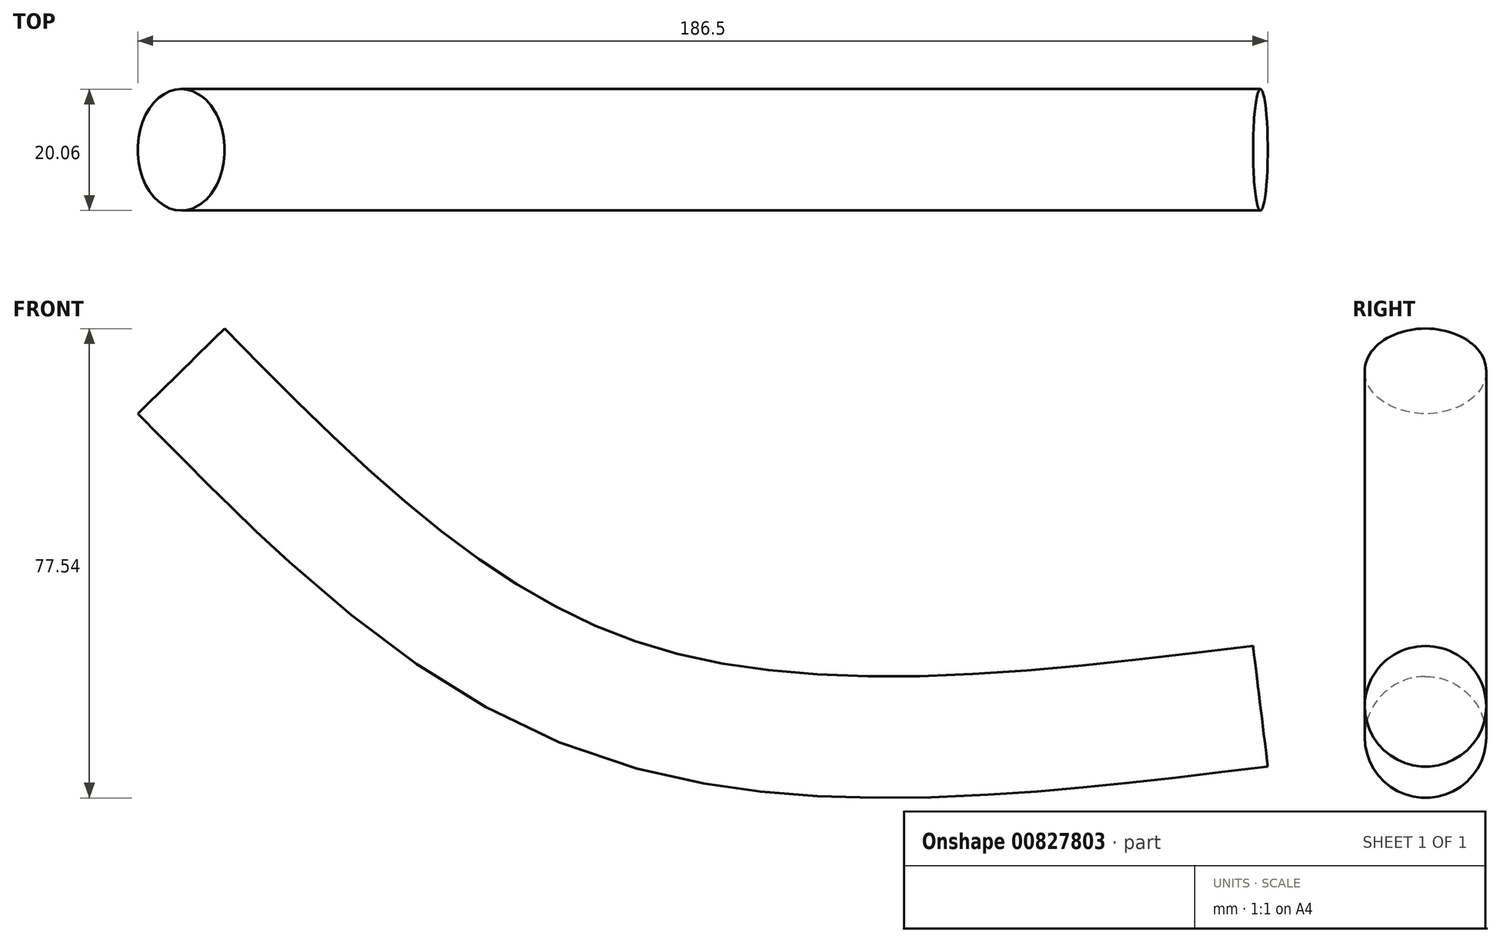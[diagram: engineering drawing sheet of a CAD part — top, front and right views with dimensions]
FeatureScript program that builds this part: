
annotation { "Feature Type Name" : "Feature", "Feature Type Description" : "" }
export const myFeature = defineFeature(function(context is Context, id is Id, definition is map)
    precondition{}
    {
        {
            var Q0;
            Q0=qCreatedBy(makeId("Front.planeOp"),FACE);
            var sketch = newSketch(context, id + "F0", { "sketchPlane" : qUnion([Q0])});
            skFitSpline(sketch, "E0", {"points": [v(97.34, 3.23) * mm, v(-9.08, 4.42) * mm, v(-81.14, 58.72) * mm], "startDerivative": vector(-218.49, -26.6) * mm, "endDerivative": vector(-137.37, 139.89) * mm});
            skSolve(sketch);
        }
        {
            var Q0;
            Q0=sQuery(id+"F0.wireOp",VERTEX,"E0.end");
            var Q1;
            Q1=sQuery(id+"F0.wireOp",EDGE,"E0");
            cPlane(context, id + "F1", {"entities" : qUnion([Q0, Q1]), "cplaneType" : CPlaneType.CURVE_POINT, "offset" : 25.4 * mm, "width" : 152.4 * mm, "height" : 152.4 * mm});
        }
        {
            var Q0;
            Q0=qCreatedBy(id+"F1.planeOp",FACE);
            var sketch = newSketch(context, id + "F2", { "sketchPlane" : qUnion([Q0])});
            skCircle(sketch, "E1", {"center": v(-16.32, 0) * mm, "radius": 10.03 * mm});
            skSolve(sketch);
        }
        {
            var Q0;
            Q0=makeQuery(id+"F2.imprint","IMPRINT",FACE,{"disambiguationData":[TD([[makeQuery(id+"F2.imprint","IMPRINT",EDGE,{"derivedFrom":sQuery(id+"F2.wireOp",EDGE,"E1")}),1.0]])]});
            var Q1;
            Q1=sQuery(id+"F0.wireOp",EDGE,"E0");
            sweep(context, id + "F3", {"profiles" : qUnion([Q0]), "path" : qUnion([Q1])});
        }
    });
